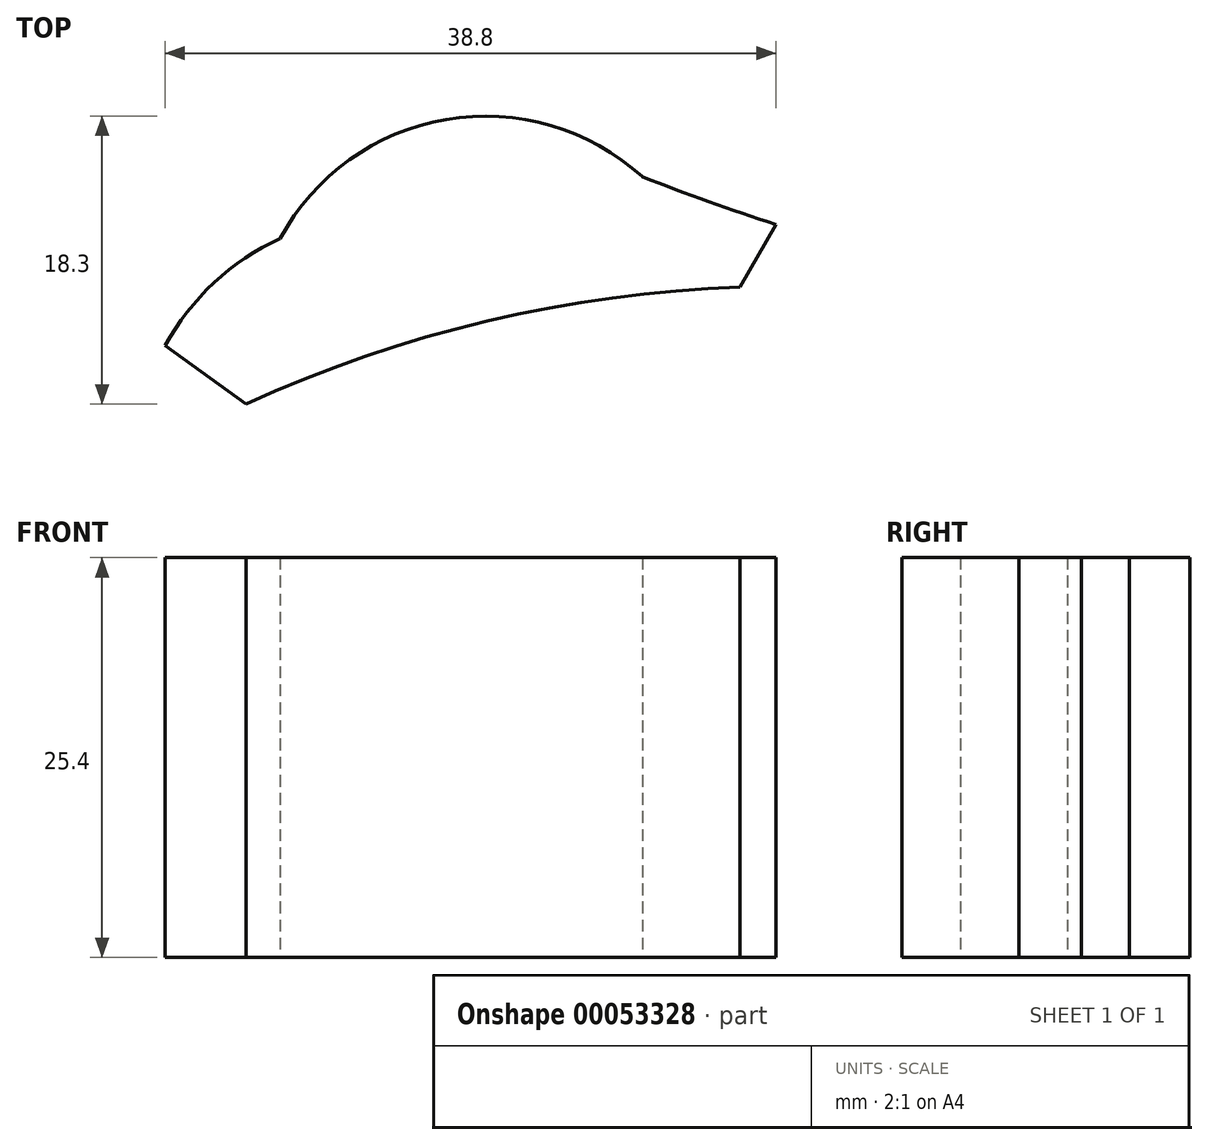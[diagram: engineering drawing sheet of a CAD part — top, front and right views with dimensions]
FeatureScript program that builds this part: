
annotation { "Feature Type Name" : "Feature", "Feature Type Description" : "" }
export const myFeature = defineFeature(function(context is Context, id is Id, definition is map)
    precondition{}
    {
        {
            var Q0;
            Q0=qCreatedBy(makeId("Top.planeOp"),FACE);
            var sketch = newSketch(context, id + "F0", { "sketchPlane" : qUnion([Q0])});
            skPoint(sketch, "E0.center.orphan", {"position": v(-21.96, 0) * mm});
            skArc(sketch, "E1", {"start": v(4, 20.68) * mm, "mid": v(-12.06, 18.53) * mm, "end": v(-27.38, 13.26) * mm});
            skLineSegment(sketch, "E2", {"start": v(-32.52, 16.97) * mm, "end": v(-27.38, 13.26) * mm});
            skLineSegment(sketch, "E3", {"start": v(4, 20.68) * mm, "end": v(6.28, 24.67) * mm});
            skArc(sketch, "E4", {"start": v(6.28, 24.67) * mm, "mid": v(-13.76, 24.03) * mm, "end": v(-32.52, 16.97) * mm});
            skArc(sketch, "E5", {"start": v(0, 25.18) * mm, "mid": v(-15.01, 31.28) * mm, "end": v(-26.62, 19.97) * mm});
            skArc(sketch, "E6", {"start": v(-25.2, 23.78) * mm, "mid": v(-25.12, 23.92) * mm, "end": v(-25.04, 24.07) * mm});
            skPoint(sketch, "E7.end.orphan", {"position": v(-35.03, 34.25) * mm});
            skPoint(sketch, "E8.orphan", {"position": v(-32.52, 20.1) * mm});
            skArc(sketch, "E9", {"start": v(-25.2, 23.78) * mm, "mid": v(-29.4, 20.97) * mm, "end": v(-32.52, 16.97) * mm});
            skArc(sketch, "E10", {"start": v(-2.2, 27.7) * mm, "mid": v(2.01, 26.13) * mm, "end": v(6.28, 24.67) * mm});
            skSolve(sketch);
        }
        {
            var Q0;
            {var subQ0=sQuery(id+"F0.wireOp",EDGE,"E6");Q0=makeQuery(id+"F0.imprint","IMPRINT",FACE,{"disambiguationData":[TD([[makeQuery(id+"F0.imprint","IMPRINT",EDGE,{"derivedFrom":subQ0}),1.0]])]});}
            var Q1;
            {var subQ0=sQuery(id+"F0.wireOp",EDGE,"E10");Q1=makeQuery(id+"F0.imprint","IMPRINT",FACE,{"disambiguationData":[TD([[makeQuery(id+"F0.imprint","IMPRINT",EDGE,{"derivedFrom":subQ0}),-1.0]])]});}
            var Q2;
            {var subQ0=sQuery(id+"F0.wireOp",EDGE,"E9");Q2=makeQuery(id+"F0.imprint","IMPRINT",FACE,{"disambiguationData":[TD([[makeQuery(id+"F0.imprint","IMPRINT",EDGE,{"derivedFrom":subQ0}),1.0]])]});}
            var Q3;
            Q3=makeQuery(id+"F0.imprint","IMPRINT",FACE,{"disambiguationData":[TD([[makeQuery(id+"F0.imprint","IMPRINT",EDGE,{"derivedFrom":sQuery(id+"F0.wireOp",EDGE,"E1")}),-1.0]])]});
            var Q4;
            {var subQ3=sQuery(id+"F0.wireOp",EDGE,"E6");Q4=makeQuery(id+"F0.imprint","IMPRINT",FACE,{"disambiguationData":[TD([[makeQuery(id+"F0.imprint","IMPRINT",EDGE,{"derivedFrom":subQ3}),-1.0]])]});}
            extrude(context, id + "F1", {"entities" : qUnion([Q0, Q1, Q2, Q3, Q4]), "depth" : 25.4 * mm});
        }
    });
